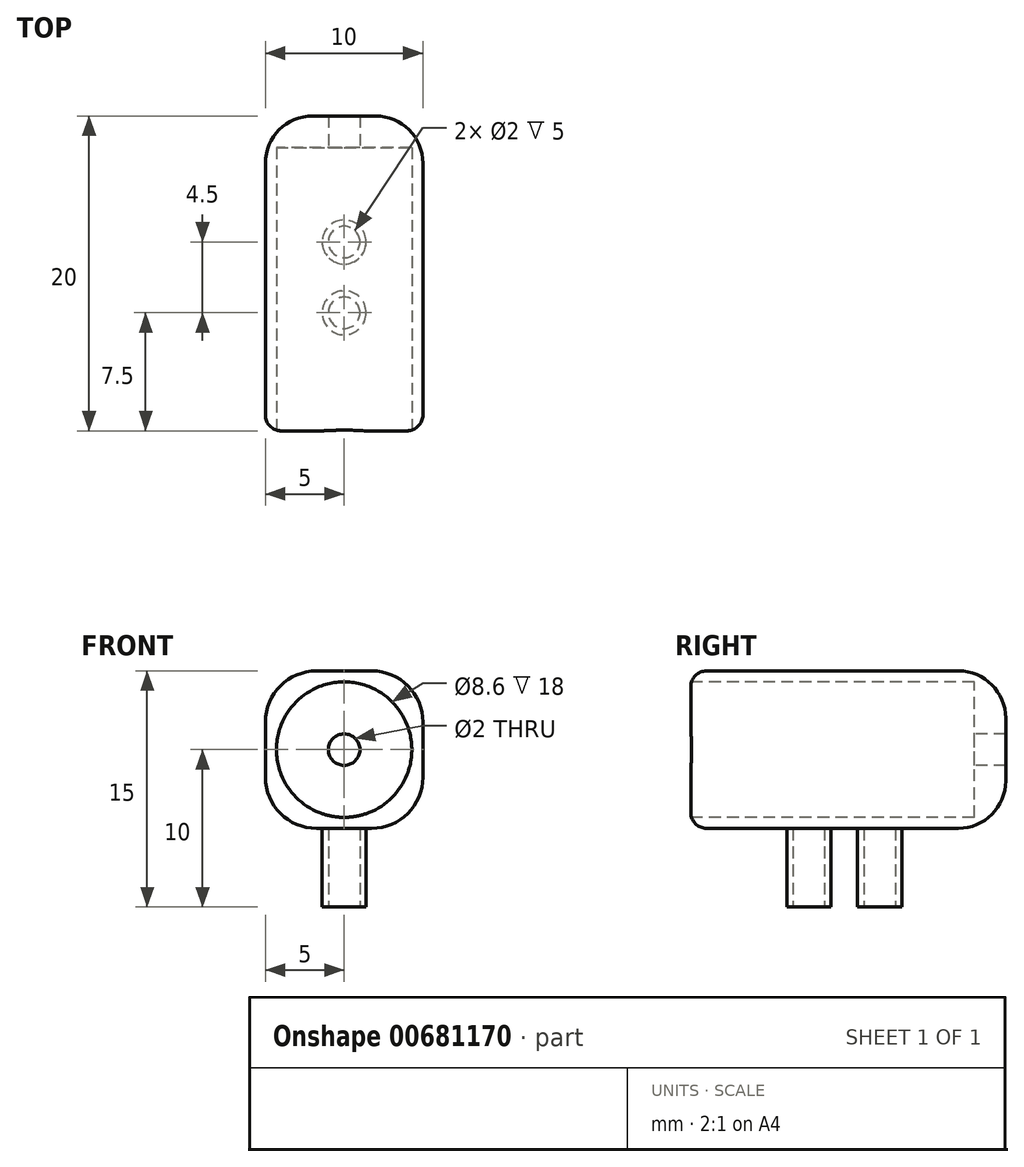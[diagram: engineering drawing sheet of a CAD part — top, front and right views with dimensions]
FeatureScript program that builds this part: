
annotation { "Feature Type Name" : "Feature", "Feature Type Description" : "" }
export const myFeature = defineFeature(function(context is Context, id is Id, definition is map)
    precondition{}
    {
        {
            var Q0;
            Q0=qCreatedBy(makeId("Front.planeOp"),FACE);
            var sketch = newSketch(context, id + "F0", { "sketchPlane" : qUnion([Q0])});
            skLineSegment(sketch, "E0.bottom", {"start": v(0, 0) * mm, "end": v(10, 0) * mm});
            skLineSegment(sketch, "E0.top", {"start": v(0, 10) * mm, "end": v(10, 10) * mm});
            skLineSegment(sketch, "E0.left", {"start": v(0, 0) * mm, "end": v(0, 10) * mm});
            skLineSegment(sketch, "E0.right", {"start": v(10, 0) * mm, "end": v(10, 10) * mm});
            skSolve(sketch);
        }
        {
            var Q0;
            Q0=qSketchRegion(id+"F0",true);
            extrude(context, id + "F1", {"entities" : qUnion([Q0]), "depth" : 20 * mm});
        }
        {
            var Q0;
            Q0=makeQuery(id+"F1.opExtrude","CAP_FACE",FACE,{"disambiguationData":[OSD([sQuery(id+"F0.wireOp",EDGE,"E0.bottom"),sQuery(id+"F0.wireOp",EDGE,"E0.top"),sQuery(id+"F0.wireOp",EDGE,"E0.left"),sQuery(id+"F0.wireOp",EDGE,"E0.right")])],"isStart":false});
            var sketch = newSketch(context, id + "F2", { "sketchPlane" : qUnion([Q0])});
            skCircle(sketch, "E1", {"center": v(5, 5) * mm, "radius": 4.3 * mm});
            skSolve(sketch);
        }
        {
            var Q0;
            Q0=qSketchRegion(id+"F2",true);
            extrude(context, id + "F3", {"entities" : qUnion([Q0]), "operationType" : NewBodyOperationType.REMOVE, "oppositeDirection" : true, "depth" : 18 * mm});
        }
        {
            var Q0;
            Q0=makeQuery(id+"F3.boolean.opBoolean","COPY",FACE,{"derivedFrom":makeQuery(id+"F3.opExtrude","CAP_FACE",FACE,{"disambiguationData":[OSD([sQuery(id+"F2.wireOp",EDGE,"E1")])],"isStart":false})});
            var sketch = newSketch(context, id + "F4", { "sketchPlane" : qUnion([Q0])});
            skCircle(sketch, "E2", {"center": v(5, 5) * mm, "radius": 1 * mm});
            skSolve(sketch);
        }
        {
            var Q0;
            Q0=qSketchRegion(id+"F4",true);
            extrude(context, id + "F5", {"entities" : qUnion([Q0]), "operationType" : NewBodyOperationType.REMOVE, "oppositeDirection" : true, "depth" : 25.4 * mm});
        }
        {
            var Q0;
            Q0=makeQuery(id+"F1.opExtrude","SWEPT_EDGE",EDGE,{"disambiguationData":[OSD([sQuery(id+"F0.wireOp",EDGE,"E0.bottom"),sQuery(id+"F0.wireOp",EDGE,"E0.right")])]});
            fillet(context, id + "F6", {"entities" : qUnion([Q0]), "radius" : 3.25 * mm, "tangentPropagation" : true, "allowEdgeOverflow" : false});
        }
        {
            var Q0;
            Q0=makeQuery(id+"F1.opExtrude","SWEPT_EDGE",EDGE,{"disambiguationData":[OSD([sQuery(id+"F0.wireOp",EDGE,"E0.bottom"),sQuery(id+"F0.wireOp",EDGE,"E0.left")])]});
            var Q1;
            Q1=makeQuery(id+"F1.opExtrude","SWEPT_EDGE",EDGE,{"disambiguationData":[OSD([sQuery(id+"F0.wireOp",EDGE,"E0.top"),sQuery(id+"F0.wireOp",EDGE,"E0.right")])]});
            var Q2;
            Q2=makeQuery(id+"F1.opExtrude","SWEPT_EDGE",EDGE,{"disambiguationData":[OSD([sQuery(id+"F0.wireOp",EDGE,"E0.top"),sQuery(id+"F0.wireOp",EDGE,"E0.left")])]});
            fillet(context, id + "F7", {"entities" : qUnion([Q0, Q1, Q2]), "radius" : 3.25 * mm, "tangentPropagation" : true, "allowEdgeOverflow" : false});
        }
        {
            var Q0;
            Q0=makeQuery(id+"F1.opExtrude","SWEPT_FACE",FACE,{"disambiguationData":[OSD([sQuery(id+"F0.wireOp",EDGE,"E0.bottom")])]});
            var sketch = newSketch(context, id + "F8", { "sketchPlane" : qUnion([Q0])});
            skCircle(sketch, "E3", {"center": v(5, 12.5) * mm, "radius": 1.4 * mm});
            skCircle(sketch, "E4", {"center": v(5, 8) * mm, "radius": 1.4 * mm});
            skSolve(sketch);
        }
        {
            var Q0;
            Q0=qSketchRegion(id+"F8",true);
            extrude(context, id + "F9", {"entities" : qUnion([Q0]), "operationType" : NewBodyOperationType.ADD, "depth" : 5 * mm});
        }
        {
            var Q0;
            {var subQ0=sQuery(id+"F0.wireOp",EDGE,"E0.left");var subQ1=sQuery(id+"F0.wireOp",EDGE,"E0.top");Q0=makeQuery(id+"F7.opFillet","BLEND_EDGE",EDGE,{"blendedFrom":[makeQuery(id+"F1.opExtrude","SWEPT_EDGE",EDGE,{"disambiguationData":[OSD([subQ1,subQ0])]}),makeQuery(id+"F1.opExtrude","CAP_FACE",FACE,{"disambiguationData":[OSD([sQuery(id+"F0.wireOp",EDGE,"E0.bottom"),subQ1,subQ0,sQuery(id+"F0.wireOp",EDGE,"E0.right")])],"isStart":false})],"blendedInto":[makeQuery(id+"F1.opExtrude","CAP_FACE",FACE,{"disambiguationData":[OSD([sQuery(id+"F0.wireOp",EDGE,"E0.bottom"),subQ1,subQ0,sQuery(id+"F0.wireOp",EDGE,"E0.right")])],"isStart":false})]});}
            var Q1;
            Q1=makeQuery(id+"F1.opExtrude","CAP_EDGE",EDGE,{"disambiguationData":[OSD([sQuery(id+"F0.wireOp",EDGE,"E0.left")])],"isStart":false});
            var Q2;
            {var subQ0=sQuery(id+"F0.wireOp",EDGE,"E0.left");var subQ1=sQuery(id+"F0.wireOp",EDGE,"E0.bottom");Q2=makeQuery(id+"F7.opFillet","BLEND_EDGE",EDGE,{"blendedFrom":[makeQuery(id+"F1.opExtrude","SWEPT_EDGE",EDGE,{"disambiguationData":[OSD([subQ1,subQ0])]}),makeQuery(id+"F1.opExtrude","CAP_FACE",FACE,{"disambiguationData":[OSD([subQ1,sQuery(id+"F0.wireOp",EDGE,"E0.top"),subQ0,sQuery(id+"F0.wireOp",EDGE,"E0.right")])],"isStart":false})],"blendedInto":[makeQuery(id+"F1.opExtrude","CAP_FACE",FACE,{"disambiguationData":[OSD([subQ1,sQuery(id+"F0.wireOp",EDGE,"E0.top"),subQ0,sQuery(id+"F0.wireOp",EDGE,"E0.right")])],"isStart":false})]});}
            var Q3;
            Q3=makeQuery(id+"F1.opExtrude","CAP_EDGE",EDGE,{"disambiguationData":[OSD([sQuery(id+"F0.wireOp",EDGE,"E0.bottom")])],"isStart":false});
            var Q4;
            {var subQ0=sQuery(id+"F0.wireOp",EDGE,"E0.right");var subQ1=sQuery(id+"F0.wireOp",EDGE,"E0.bottom");Q4=makeQuery(id+"F6.opFillet","BLEND_EDGE",EDGE,{"blendedFrom":[makeQuery(id+"F1.opExtrude","SWEPT_EDGE",EDGE,{"disambiguationData":[OSD([subQ1,subQ0])]}),makeQuery(id+"F1.opExtrude","CAP_FACE",FACE,{"disambiguationData":[OSD([subQ1,sQuery(id+"F0.wireOp",EDGE,"E0.top"),sQuery(id+"F0.wireOp",EDGE,"E0.left"),subQ0])],"isStart":false})],"blendedInto":[makeQuery(id+"F1.opExtrude","CAP_FACE",FACE,{"disambiguationData":[OSD([subQ1,sQuery(id+"F0.wireOp",EDGE,"E0.top"),sQuery(id+"F0.wireOp",EDGE,"E0.left"),subQ0])],"isStart":false})]});}
            var Q5;
            Q5=makeQuery(id+"F1.opExtrude","CAP_EDGE",EDGE,{"disambiguationData":[OSD([sQuery(id+"F0.wireOp",EDGE,"E0.right")])],"isStart":false});
            var Q6;
            {var subQ0=sQuery(id+"F0.wireOp",EDGE,"E0.right");var subQ1=sQuery(id+"F0.wireOp",EDGE,"E0.top");Q6=makeQuery(id+"F7.opFillet","BLEND_EDGE",EDGE,{"blendedFrom":[makeQuery(id+"F1.opExtrude","SWEPT_EDGE",EDGE,{"disambiguationData":[OSD([subQ1,subQ0])]}),makeQuery(id+"F1.opExtrude","CAP_FACE",FACE,{"disambiguationData":[OSD([sQuery(id+"F0.wireOp",EDGE,"E0.bottom"),subQ1,sQuery(id+"F0.wireOp",EDGE,"E0.left"),subQ0])],"isStart":false})],"blendedInto":[makeQuery(id+"F1.opExtrude","CAP_FACE",FACE,{"disambiguationData":[OSD([sQuery(id+"F0.wireOp",EDGE,"E0.bottom"),subQ1,sQuery(id+"F0.wireOp",EDGE,"E0.left"),subQ0])],"isStart":false})]});}
            var Q7;
            Q7=makeQuery(id+"F1.opExtrude","CAP_EDGE",EDGE,{"disambiguationData":[OSD([sQuery(id+"F0.wireOp",EDGE,"E0.top")])],"isStart":false});
            fillet(context, id + "F10", {"entities" : qUnion([Q0, Q1, Q2, Q3, Q4, Q5, Q6, Q7]), "radius" : 1 * mm, "tangentPropagation" : true, "allowEdgeOverflow" : false});
        }
        {
            var Q0;
            Q0=makeQuery(id+"F1.opExtrude","CAP_EDGE",EDGE,{"disambiguationData":[OSD([sQuery(id+"F0.wireOp",EDGE,"E0.right")])],"isStart":true});
            var Q1;
            {var subQ0=sQuery(id+"F0.wireOp",EDGE,"E0.right");var subQ1=sQuery(id+"F0.wireOp",EDGE,"E0.bottom");Q1=makeQuery(id+"F6.opFillet","BLEND_EDGE",EDGE,{"blendedFrom":[makeQuery(id+"F1.opExtrude","SWEPT_EDGE",EDGE,{"disambiguationData":[OSD([subQ1,subQ0])]}),makeQuery(id+"F1.opExtrude","CAP_FACE",FACE,{"disambiguationData":[OSD([subQ1,sQuery(id+"F0.wireOp",EDGE,"E0.top"),sQuery(id+"F0.wireOp",EDGE,"E0.left"),subQ0])],"isStart":true})],"blendedInto":[makeQuery(id+"F1.opExtrude","CAP_FACE",FACE,{"disambiguationData":[OSD([subQ1,sQuery(id+"F0.wireOp",EDGE,"E0.top"),sQuery(id+"F0.wireOp",EDGE,"E0.left"),subQ0])],"isStart":true})]});}
            var Q2;
            Q2=makeQuery(id+"F1.opExtrude","CAP_EDGE",EDGE,{"disambiguationData":[OSD([sQuery(id+"F0.wireOp",EDGE,"E0.bottom")])],"isStart":true});
            var Q3;
            {var subQ0=sQuery(id+"F0.wireOp",EDGE,"E0.left");var subQ1=sQuery(id+"F0.wireOp",EDGE,"E0.bottom");Q3=makeQuery(id+"F7.opFillet","BLEND_EDGE",EDGE,{"blendedFrom":[makeQuery(id+"F1.opExtrude","SWEPT_EDGE",EDGE,{"disambiguationData":[OSD([subQ1,subQ0])]}),makeQuery(id+"F1.opExtrude","CAP_FACE",FACE,{"disambiguationData":[OSD([subQ1,sQuery(id+"F0.wireOp",EDGE,"E0.top"),subQ0,sQuery(id+"F0.wireOp",EDGE,"E0.right")])],"isStart":true})],"blendedInto":[makeQuery(id+"F1.opExtrude","CAP_FACE",FACE,{"disambiguationData":[OSD([subQ1,sQuery(id+"F0.wireOp",EDGE,"E0.top"),subQ0,sQuery(id+"F0.wireOp",EDGE,"E0.right")])],"isStart":true})]});}
            var Q4;
            Q4=makeQuery(id+"F1.opExtrude","CAP_EDGE",EDGE,{"disambiguationData":[OSD([sQuery(id+"F0.wireOp",EDGE,"E0.left")])],"isStart":true});
            var Q5;
            {var subQ0=sQuery(id+"F0.wireOp",EDGE,"E0.left");var subQ1=sQuery(id+"F0.wireOp",EDGE,"E0.top");Q5=makeQuery(id+"F7.opFillet","BLEND_EDGE",EDGE,{"blendedFrom":[makeQuery(id+"F1.opExtrude","SWEPT_EDGE",EDGE,{"disambiguationData":[OSD([subQ1,subQ0])]}),makeQuery(id+"F1.opExtrude","CAP_FACE",FACE,{"disambiguationData":[OSD([sQuery(id+"F0.wireOp",EDGE,"E0.bottom"),subQ1,subQ0,sQuery(id+"F0.wireOp",EDGE,"E0.right")])],"isStart":true})],"blendedInto":[makeQuery(id+"F1.opExtrude","CAP_FACE",FACE,{"disambiguationData":[OSD([sQuery(id+"F0.wireOp",EDGE,"E0.bottom"),subQ1,subQ0,sQuery(id+"F0.wireOp",EDGE,"E0.right")])],"isStart":true})]});}
            var Q6;
            Q6=makeQuery(id+"F1.opExtrude","CAP_EDGE",EDGE,{"disambiguationData":[OSD([sQuery(id+"F0.wireOp",EDGE,"E0.top")])],"isStart":true});
            var Q7;
            {var subQ0=sQuery(id+"F0.wireOp",EDGE,"E0.right");var subQ1=sQuery(id+"F0.wireOp",EDGE,"E0.top");Q7=makeQuery(id+"F7.opFillet","BLEND_EDGE",EDGE,{"blendedFrom":[makeQuery(id+"F1.opExtrude","SWEPT_EDGE",EDGE,{"disambiguationData":[OSD([subQ1,subQ0])]}),makeQuery(id+"F1.opExtrude","CAP_FACE",FACE,{"disambiguationData":[OSD([sQuery(id+"F0.wireOp",EDGE,"E0.bottom"),subQ1,sQuery(id+"F0.wireOp",EDGE,"E0.left"),subQ0])],"isStart":true})],"blendedInto":[makeQuery(id+"F1.opExtrude","CAP_FACE",FACE,{"disambiguationData":[OSD([sQuery(id+"F0.wireOp",EDGE,"E0.bottom"),subQ1,sQuery(id+"F0.wireOp",EDGE,"E0.left"),subQ0])],"isStart":true})]});}
            fillet(context, id + "F11", {"entities" : qUnion([Q0, Q1, Q2, Q3, Q4, Q5, Q6, Q7]), "radius" : 3 * mm, "tangentPropagation" : true, "allowEdgeOverflow" : false});
        }
        {
            var Q0;
            Q0=makeQuery(id+"F9.opExtrude","CAP_FACE",FACE,{"disambiguationData":[OSD([sQuery(id+"F8.wireOp",EDGE,"E3")])],"isStart":false});
            var sketch = newSketch(context, id + "F12", { "sketchPlane" : qUnion([Q0])});
            skCircle(sketch, "E5", {"center": v(5, 12.5) * mm, "radius": 1 * mm});
            skCircle(sketch, "E6", {"center": v(5, 8) * mm, "radius": 1 * mm});
            skSolve(sketch);
        }
        {
            var Q0;
            Q0=qSketchRegion(id+"F12",true);
            extrude(context, id + "F13", {"entities" : qUnion([Q0]), "operationType" : NewBodyOperationType.REMOVE, "oppositeDirection" : true, "depth" : 5 * mm, "offsetDistance" : 25.4 * mm});
        }
    });
